# Revit family: PRD_FrankeWS_WtrSplySystmsCtrl_ElectronicModule_ZAQUA030
name_source: partatom
category: Electrical Equipment
revit_build: Autodesk Revit 2018 (Build: 20190510_1515(x64)
units: mm (PartAtom-declared; Revit-internal decimal feet)

## family parameters
Always vertical = Yes
Cut with Voids When Loaded = No
OmniClass Number = 23.45.55.11
OmniClass Title = Sanitary Components
Part Type = Equipment Switch
Room Calculation Point = No
Round Connector Dimension = Use Diameter
Shared = No
Work Plane-Based = No

## types (1)
- ZAQUA030
    AssetType = Fixed
    BIMObjectName = PRD_AR_WaterSupplySystemsControl_ElectronicModule_ZAQUA030
    Category = Ss_75_70_52_96, Water supply control systems
    Description = Electronic module - A3000 open, for circulation line. For ensuring thermal treatment of the circulation line. Time and temperature values can be parameterized specifically to building requirements with corresponding software. Including electronic T-junction and 2 clip-on temperature sensors with 1.5 m extension cable.
    DurationUnit = year
    ElectricalDeviceNominalPower = 0 W
    ElectronicModuleMaterial = <By Category>
    GrossWeight = 0.60 kg
    HasProtectiveEarth = Yes
    IP_Code = 68
    IfcExportAs = IfcDistributionElement
    IfcExportType = NOTDEFINED
    InsulationStandardClass = NotKnown
    Manufacturer = KWC Group AG
    ManufacturerName = KWC Group AG
    ManufacturerURL = www.kwc.com
    Model = ZAQUA030
    ModelNumber = 2000101183
    ModelReference = ZAQUA030
    NBSDescription = Water supply systems control
    NBSReference = 75-75-50/110
    Name = Electronic module ZAQUA030
    NetWeight = 0.42 kg
    NominalCurrent = 0 A
    NominalFrequencyRange = 50
    NominalHeight = 0 mm  [stored 0 ft]
    NominalLength = 0 mm  [stored 0 ft]
    NominalVoltage = 24
    NominalWidth = 0 mm  [stored 0 ft]
    NumberOfPoles = 1
    PhaseAngle = 0.00°
    PhaseReference = 0
    ProductInformation = https://pim.kwc.com
    URL = www.kwc.com
    Uniclass2015Code = Ss_75_70_52_96
    Uniclass2015Title = Water supply control systems
    Uniclass2015Version = Systems v1.7
    UsageCurrent = 0 A
    Version = 1
    Voltage = 24
    WarrantyDurationUnit = year

note: [stored X ft] marks values corroborated as IEEE doubles in the binary element streams (Revit-internal decimal feet)

## geometry (parser evidence)
native form markers: Sweep x3
no freeform markers — native parametric forms only
